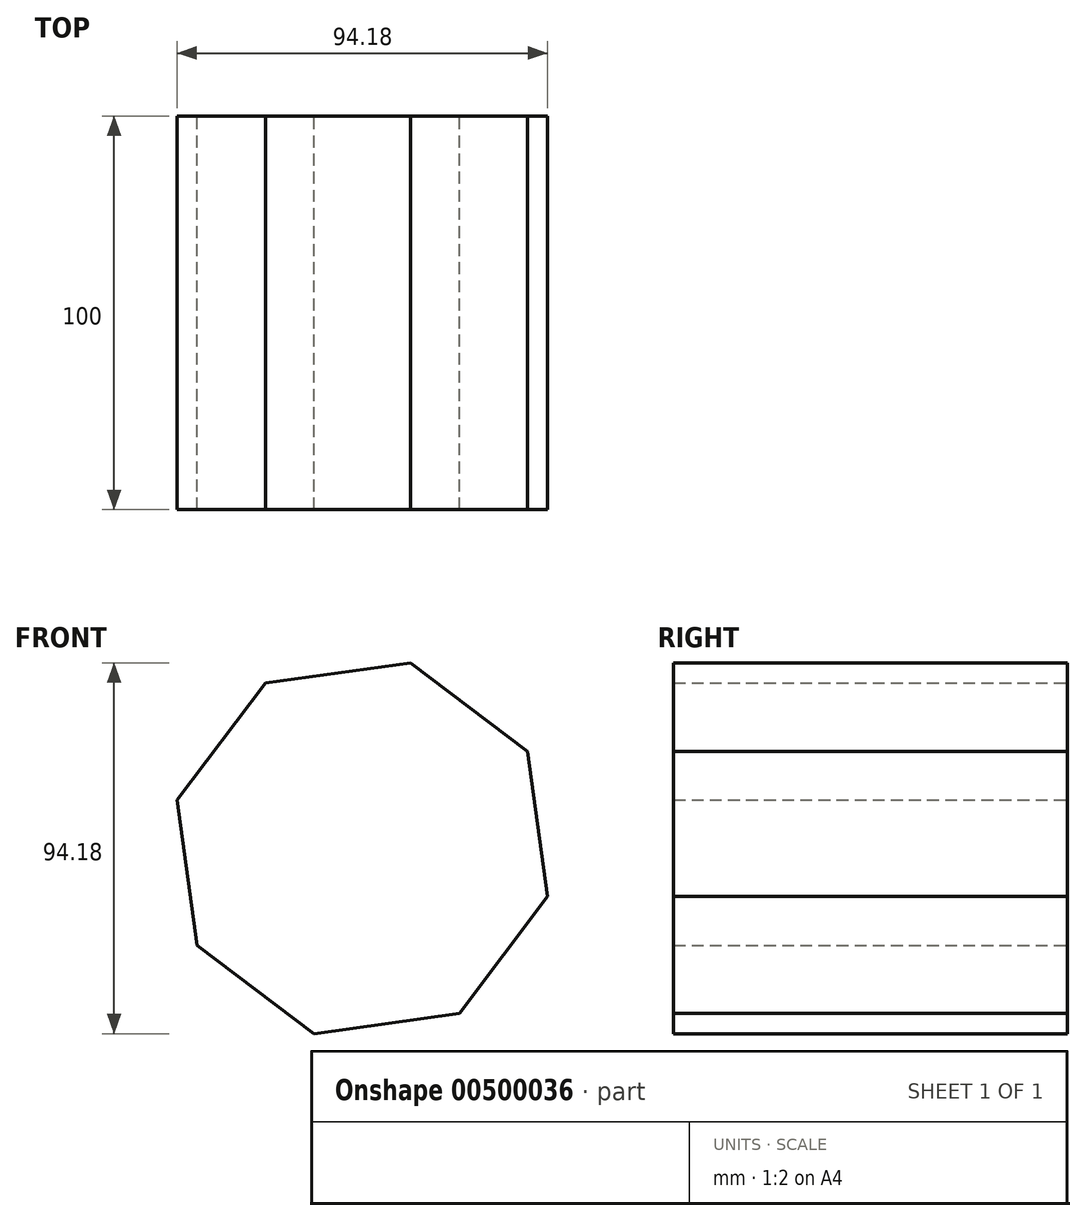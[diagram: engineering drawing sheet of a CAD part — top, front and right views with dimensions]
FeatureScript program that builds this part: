
annotation { "Feature Type Name" : "Feature", "Feature Type Description" : "" }
export const myFeature = defineFeature(function(context is Context, id is Id, definition is map)
    precondition{}
    {
        {
            var Q0;
            Q0=qCreatedBy(makeId("Front.planeOp"),FACE);
            var sketch = newSketch(context, id + "F0", { "sketchPlane" : qUnion([Q0])});
            skCircle(sketch, "E0.cCircle", {"center": v(0, 0) * mm, "radius": 48.67 * mm, "construction": true});
            skLineSegment(sketch, "E0.0", {"start": v(41.97, 24.63) * mm, "end": v(47.1, -12.26) * mm});
            skLineSegment(sketch, "E0.1", {"start": v(47.1, -12.26) * mm, "end": v(24.63, -41.97) * mm});
            skLineSegment(sketch, "E0.2", {"start": v(24.63, -41.97) * mm, "end": v(-12.26, -47.1) * mm});
            skLineSegment(sketch, "E0.3", {"start": v(-12.26, -47.1) * mm, "end": v(-41.97, -24.63) * mm});
            skLineSegment(sketch, "E0.4", {"start": v(-41.97, -24.63) * mm, "end": v(-47.1, 12.26) * mm});
            skLineSegment(sketch, "E0.5", {"start": v(-47.1, 12.26) * mm, "end": v(-24.63, 41.97) * mm});
            skLineSegment(sketch, "E0.6", {"start": v(-24.63, 41.97) * mm, "end": v(12.26, 47.1) * mm});
            skLineSegment(sketch, "E0.7", {"start": v(12.26, 47.1) * mm, "end": v(41.97, 24.63) * mm});
            skSolve(sketch);
        }
        {
            var Q0;
            Q0 = qSketchRegion(id + "F0", true);
            extrude(context, id + "F1", {"entities" : qUnion([Q0]), "endBound" : BoundingType.SYMMETRIC, "depth" : 100 * mm});
        }
    });
